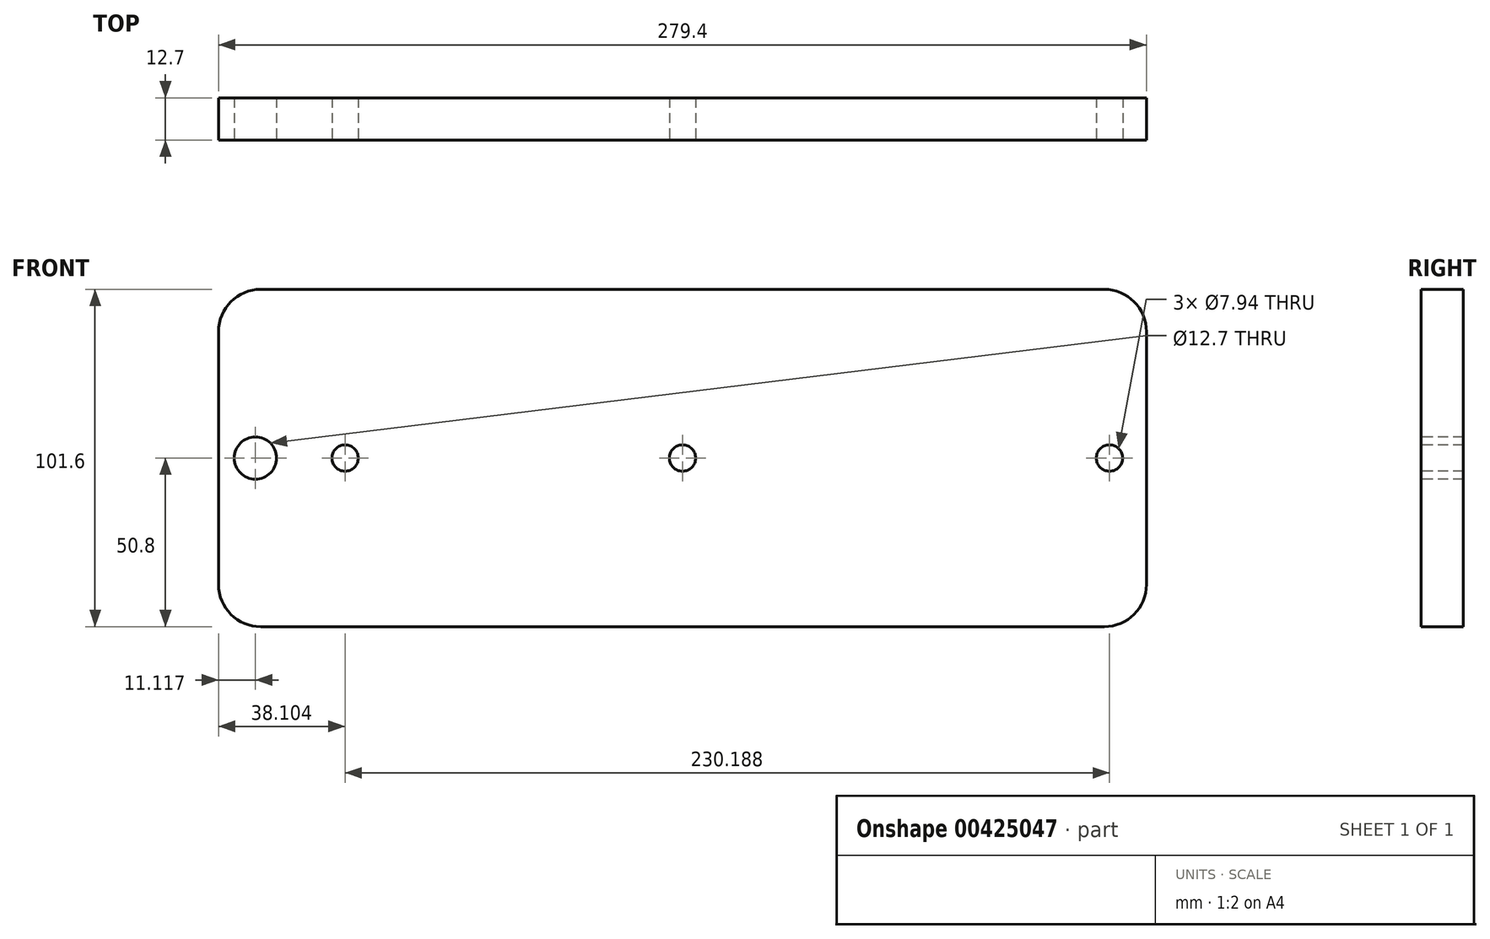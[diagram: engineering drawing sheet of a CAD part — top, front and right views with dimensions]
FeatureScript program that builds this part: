
annotation { "Feature Type Name" : "Feature", "Feature Type Description" : "" }
export const myFeature = defineFeature(function(context is Context, id is Id, definition is map)
    precondition{}
    {
        {
            var Q0;
            Q0=qCreatedBy(makeId("Front.planeOp"),FACE);
            var sketch = newSketch(context, id + "F0", { "sketchPlane" : qUnion([Q0])});
            skLineSegment(sketch, "E0", {"start": v(-77.3, 0) * mm, "end": v(202.1, 0) * mm});
            skLineSegment(sketch, "E1", {"start": v(202.1, 0) * mm, "end": v(202.1, 101.6) * mm});
            skLineSegment(sketch, "E2", {"start": v(202.1, 101.6) * mm, "end": v(-77.3, 101.6) * mm});
            skLineSegment(sketch, "E3", {"start": v(-77.3, 101.6) * mm, "end": v(-77.3, 0) * mm});
            skSolve(sketch);
        }
        {
            var Q0;
            Q0=makeQuery(id+"F0.imprint","IMPRINT",FACE,{"disambiguationData":[TD([[makeQuery(id+"F0.imprint","IMPRINT",EDGE,{"derivedFrom":sQuery(id+"F0.wireOp",EDGE,"E0")}),1.0]])]});
            extrude(context, id + "F1", {"entities" : qUnion([Q0]), "depth" : 12.7 * mm});
        }
        {
            var Q0;
            Q0=makeQuery(id+"F1.opExtrude","SWEPT_EDGE",EDGE,{"disambiguationData":[OSD([sQuery(id+"F0.wireOp",EDGE,"E2"),sQuery(id+"F0.wireOp",EDGE,"E3")])]});
            var Q1;
            Q1=makeQuery(id+"F1.opExtrude","SWEPT_EDGE",EDGE,{"disambiguationData":[OSD([sQuery(id+"F0.wireOp",EDGE,"E0"),sQuery(id+"F0.wireOp",EDGE,"E3")])]});
            var Q2;
            Q2=makeQuery(id+"F1.opExtrude","SWEPT_EDGE",EDGE,{"disambiguationData":[OSD([sQuery(id+"F0.wireOp",EDGE,"E1"),sQuery(id+"F0.wireOp",EDGE,"E2")])]});
            var Q3;
            Q3=makeQuery(id+"F1.opExtrude","SWEPT_EDGE",EDGE,{"disambiguationData":[OSD([sQuery(id+"F0.wireOp",EDGE,"E0"),sQuery(id+"F0.wireOp",EDGE,"E1")])]});
            fillet(context, id + "F2", {"entities" : qUnion([Q0, Q1, Q2, Q3]), "radius" : 12.7 * mm, "tangentPropagation" : true, "allowEdgeOverflow" : false});
        }
        {
            var Q0;
            Q0=makeQuery(id+"F1.opExtrude","CAP_FACE",FACE,{"disambiguationData":[OSD([sQuery(id+"F0.wireOp",EDGE,"E0"),sQuery(id+"F0.wireOp",EDGE,"E1"),sQuery(id+"F0.wireOp",EDGE,"E2"),sQuery(id+"F0.wireOp",EDGE,"E3")])],"isStart":false});
            var sketch = newSketch(context, id + "F3", { "sketchPlane" : qUnion([Q0])});
            skLineSegment(sketch, "E4", {"start": v(-77.3, 0) * mm, "end": v(62.4, 0) * mm});
            skLineSegment(sketch, "E5", {"start": v(62.4, 0) * mm, "end": v(62.4, 101.6) * mm});
            skPoint(sketch, "E6", {"position": v(62.4, 50.8) * mm});
            skSolve(sketch);
        }
        {
            var Q0;
            Q0=sQuery(id+"F3.wireOp",VERTEX,"E6");
            var Q1;
            Q1=makeQuery(id+"F1.opExtrude","SWEPT_BODY",BODY,{"disambiguationData":[OSD([sQuery(id+"F0.wireOp",EDGE,"E0"),sQuery(id+"F0.wireOp",EDGE,"E1"),sQuery(id+"F0.wireOp",EDGE,"E2"),sQuery(id+"F0.wireOp",EDGE,"E3")])]});
            hole(context, id + "F4", {"style" : HoleStyle.SIMPLE, "endStyle" : HoleEndStyle.THROUGH, "holeDiameter" : 7.94 * mm, "isTappedThrough" : true, "tappedDepth" : 12.7 * mm, "tapClearance" : 3, "locations" : qUnion([Q0]), "scope" : qUnion([Q1])});
        }
        {
            var Q0;
            Q0=makeQuery(id+"F1.opExtrude","CAP_FACE",FACE,{"disambiguationData":[OSD([sQuery(id+"F0.wireOp",EDGE,"E0"),sQuery(id+"F0.wireOp",EDGE,"E1"),sQuery(id+"F0.wireOp",EDGE,"E2"),sQuery(id+"F0.wireOp",EDGE,"E3")])],"isStart":false});
            var sketch = newSketch(context, id + "F5", { "sketchPlane" : qUnion([Q0])});
            skLineSegment(sketch, "E7", {"start": v(202.1, 50.8) * mm, "end": v(190.98, 50.8) * mm});
            skLineSegment(sketch, "E8", {"start": v(190.98, 50.8) * mm, "end": v(202.1, 50.8) * mm});
            skPoint(sketch, "E9", {"position": v(190.98, 50.8) * mm});
            skLineSegment(sketch, "E10", {"start": v(-77.3, 50.8) * mm, "end": v(-39.2, 50.8) * mm});
            skLineSegment(sketch, "E11", {"start": v(-39.2, 50.8) * mm, "end": v(-77.3, 50.8) * mm});
            skLineSegment(sketch, "E12", {"start": v(-77.3, 50.8) * mm, "end": v(-66.2, 50.8) * mm});
            skLineSegment(sketch, "E13", {"start": v(-66.2, 50.8) * mm, "end": v(-77.3, 50.8) * mm});
            skSolve(sketch);
        }
        {
            var Q0;
            Q0=sQuery(id+"F5.wireOp",VERTEX,"E9");
            var Q1;
            Q1=sQuery(id+"F5.wireOp",VERTEX,"E10.end");
            var Q2;
            Q2=makeQuery(id+"F1.opExtrude","SWEPT_BODY",BODY,{"disambiguationData":[OSD([sQuery(id+"F0.wireOp",EDGE,"E0"),sQuery(id+"F0.wireOp",EDGE,"E1"),sQuery(id+"F0.wireOp",EDGE,"E2"),sQuery(id+"F0.wireOp",EDGE,"E3")])]});
            hole(context, id + "F6", {"style" : HoleStyle.SIMPLE, "endStyle" : HoleEndStyle.THROUGH, "holeDiameter" : 7.94 * mm, "isTappedThrough" : true, "tappedDepth" : 12.7 * mm, "tapClearance" : 3, "locations" : qUnion([Q0, Q1]), "scope" : qUnion([Q2])});
        }
        {
            var Q0;
            Q0=makeQuery(id+"F1.opExtrude","CAP_FACE",FACE,{"disambiguationData":[OSD([sQuery(id+"F0.wireOp",EDGE,"E0"),sQuery(id+"F0.wireOp",EDGE,"E1"),sQuery(id+"F0.wireOp",EDGE,"E2"),sQuery(id+"F0.wireOp",EDGE,"E3")])],"isStart":false});
            var sketch = newSketch(context, id + "F7", { "sketchPlane" : qUnion([Q0])});
            skLineSegment(sketch, "E14", {"start": v(-77.3, 50.8) * mm, "end": v(-66.2, 50.8) * mm});
            skSolve(sketch);
        }
        {
            var Q0;
            Q0=sQuery(id+"F7.wireOp",VERTEX,"E14.end");
            var Q1;
            Q1=makeQuery(id+"F1.opExtrude","SWEPT_BODY",BODY,{"disambiguationData":[OSD([sQuery(id+"F0.wireOp",EDGE,"E0"),sQuery(id+"F0.wireOp",EDGE,"E1"),sQuery(id+"F0.wireOp",EDGE,"E2"),sQuery(id+"F0.wireOp",EDGE,"E3")])]});
            hole(context, id + "F8", {"style" : HoleStyle.SIMPLE, "endStyle" : HoleEndStyle.THROUGH, "holeDiameter" : 12.7 * mm, "isTappedThrough" : true, "tappedDepth" : 12.7 * mm, "tapClearance" : 3, "locations" : qUnion([Q0]), "scope" : qUnion([Q1])});
        }
    });
